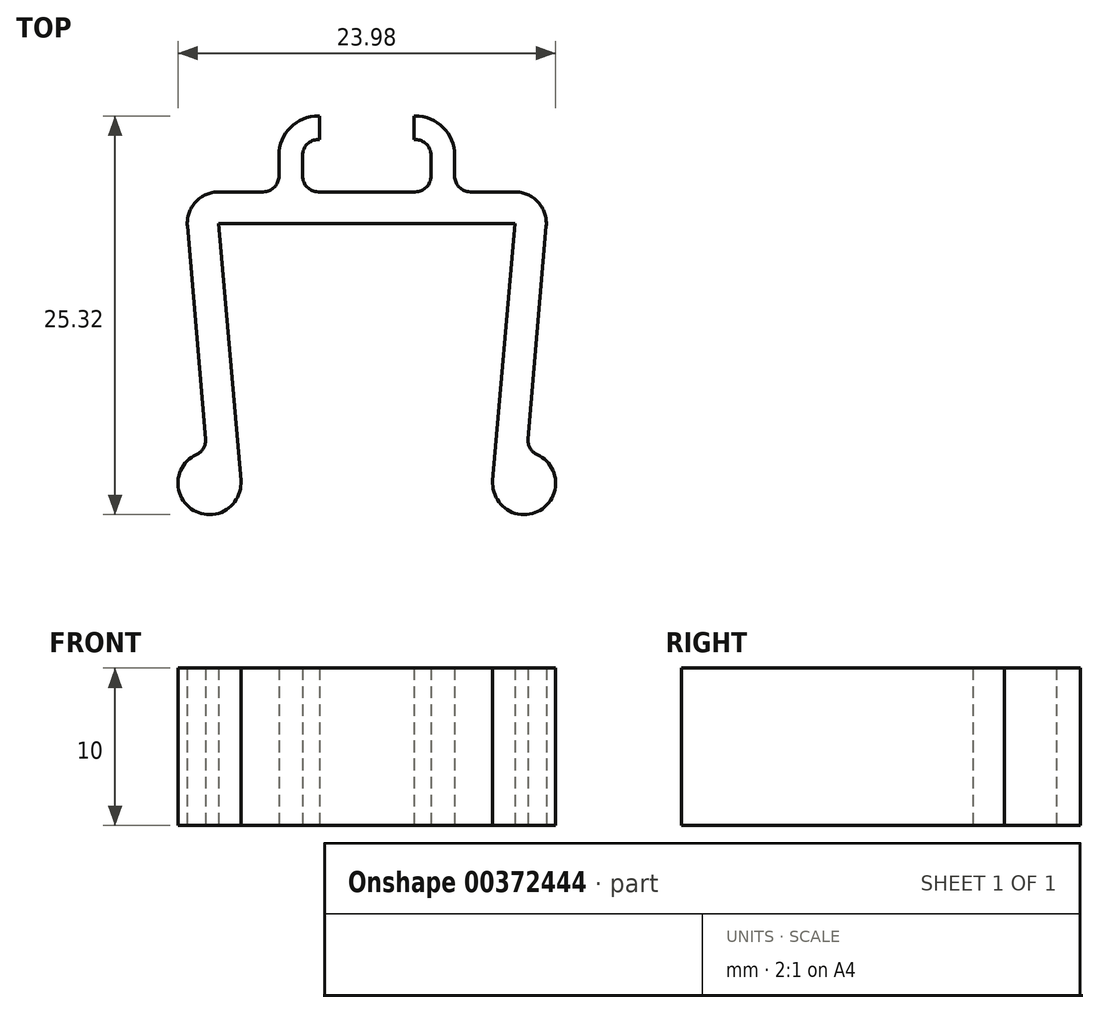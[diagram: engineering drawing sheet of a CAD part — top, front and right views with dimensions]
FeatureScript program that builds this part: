
annotation { "Feature Type Name" : "Feature", "Feature Type Description" : "" }
export const myFeature = defineFeature(function(context is Context, id is Id, definition is map)
    precondition{}
    {
        {
            var Q0;
            Q0=qCreatedBy(makeId("Top.planeOp"),FACE);
            var sketch = newSketch(context, id + "F0", { "sketchPlane" : qUnion([Q0])});
            skLineSegment(sketch, "E0.top", {"start": v(9.4, 7.19) * mm, "end": v(0, 7.19) * mm});
            skPoint(sketch, "E0.middle", {"position": v(0, 0) * mm});
            skLineSegment(sketch, "E1", {"start": v(0, 8.45) * mm, "end": v(0, -6.18) * mm, "construction": true});
            skLineSegment(sketch, "E2.MirrorCS", {"start": v(-9.4, 7.19) * mm, "end": v(0, 7.19) * mm});
            skLineSegment(sketch, "E3", {"start": v(9.4, 7.19) * mm, "end": v(8, -9.14) * mm});
            skLineSegment(sketch, "E4", {"start": v(0, 9.19) * mm, "end": v(3.08, 9.19) * mm});
            skLineSegment(sketch, "E5", {"start": v(11.4, 7.02) * mm, "end": v(10.23, -6.5) * mm});
            skArc(sketch, "E6", {"start": v(8, -9.14) * mm, "mid": v(11, -11.04) * mm, "end": v(10.82, -7.49) * mm});
            skPoint(sketch, "E7.visualSharp", {"position": v(11.58, 9.19) * mm});
            skArc(sketch, "E7.filletArc", {"start": v(11.4, 7.02) * mm, "mid": v(10.87, 8.54) * mm, "end": v(9.4, 9.19) * mm});
            skArc(sketch, "E8.MirrorCS", {"start": v(-8, -9.14) * mm, "mid": v(-11, -11.04) * mm, "end": v(-10.82, -7.49) * mm});
            skLineSegment(sketch, "E9.MirrorCS", {"start": v(-9.4, 7.19) * mm, "end": v(-8, -9.14) * mm});
            skLineSegment(sketch, "E10.MirrorCS", {"start": v(0, 9.19) * mm, "end": v(-3.08, 9.19) * mm});
            skLineSegment(sketch, "E11.MirrorCS", {"start": v(-11.4, 7.02) * mm, "end": v(-10.23, -6.5) * mm});
            skArc(sketch, "E12.MirrorCS", {"start": v(-11.4, 7.02) * mm, "mid": v(-10.87, 8.54) * mm, "end": v(-9.4, 9.19) * mm});
            skLineSegment(sketch, "E13", {"start": v(4.08, 10.19) * mm, "end": v(4.08, 11.51) * mm});
            skLineSegment(sketch, "E14", {"start": v(3.08, 12.51) * mm, "end": v(3, 12.51) * mm});
            skLineSegment(sketch, "E15", {"start": v(3, 12.51) * mm, "end": v(3, 14.01) * mm});
            skLineSegment(sketch, "E16", {"start": v(3, 14.01) * mm, "end": v(3.08, 14.01) * mm});
            skLineSegment(sketch, "E17", {"start": v(5.58, 11.51) * mm, "end": v(5.58, 10.19) * mm});
            skLineSegment(sketch, "E18.trimOffspring", {"start": v(6.58, 9.19) * mm, "end": v(9.4, 9.19) * mm});
            skPoint(sketch, "E19.visualSharp", {"position": v(5.58, 14.01) * mm});
            skArc(sketch, "E19.filletArc", {"start": v(5.58, 11.51) * mm, "mid": v(4.85, 13.28) * mm, "end": v(3.08, 14.01) * mm});
            skArc(sketch, "E20.filletArc", {"start": v(4.08, 11.51) * mm, "mid": v(3.78, 12.22) * mm, "end": v(3.08, 12.51) * mm});
            skLineSegment(sketch, "E21.MirrorCS", {"start": v(-3, 12.51) * mm, "end": v(-3, 14.01) * mm});
            skLineSegment(sketch, "E22.MirrorCS", {"start": v(-3, 14.01) * mm, "end": v(-3.08, 14.01) * mm});
            skLineSegment(sketch, "E23.MirrorCS", {"start": v(-3.08, 12.51) * mm, "end": v(-3, 12.51) * mm});
            skArc(sketch, "E24.MirrorCS", {"start": v(-4.08, 11.51) * mm, "mid": v(-3.78, 12.22) * mm, "end": v(-3.08, 12.51) * mm});
            skArc(sketch, "E25.MirrorCS", {"start": v(-5.58, 11.51) * mm, "mid": v(-4.85, 13.28) * mm, "end": v(-3.08, 14.01) * mm});
            skLineSegment(sketch, "E26.MirrorCS", {"start": v(-4.08, 10.19) * mm, "end": v(-4.08, 11.51) * mm});
            skLineSegment(sketch, "E27.MirrorCS", {"start": v(-5.58, 11.51) * mm, "end": v(-5.58, 10.19) * mm});
            skLineSegment(sketch, "E28.trimOffspring", {"start": v(-6.58, 9.19) * mm, "end": v(-9.4, 9.19) * mm});
            skPoint(sketch, "E29.visualSharp", {"position": v(-4.08, 9.19) * mm});
            skArc(sketch, "E29.filletArc", {"start": v(-4.08, 10.19) * mm, "mid": v(-3.78, 9.48) * mm, "end": v(-3.08, 9.19) * mm});
            skPoint(sketch, "E30.visualSharp", {"position": v(4.08, 9.19) * mm});
            skArc(sketch, "E30.filletArc", {"start": v(3.08, 9.19) * mm, "mid": v(3.78, 9.48) * mm, "end": v(4.08, 10.19) * mm});
            skPoint(sketch, "E31.visualSharp", {"position": v(5.58, 9.19) * mm});
            skArc(sketch, "E31.filletArc", {"start": v(5.58, 10.19) * mm, "mid": v(5.87, 9.48) * mm, "end": v(6.58, 9.19) * mm});
            skPoint(sketch, "E32.visualSharp", {"position": v(-5.58, 9.19) * mm});
            skArc(sketch, "E32.filletArc", {"start": v(-6.58, 9.19) * mm, "mid": v(-5.87, 9.48) * mm, "end": v(-5.58, 10.19) * mm});
            skPoint(sketch, "E33.visualSharp", {"position": v(-10.16, -7.32) * mm});
            skArc(sketch, "E33.filletArc", {"start": v(-10.82, -7.49) * mm, "mid": v(-10.37, -7.08) * mm, "end": v(-10.23, -6.5) * mm});
            skPoint(sketch, "E34.visualSharp", {"position": v(10.16, -7.32) * mm});
            skArc(sketch, "E34.filletArc", {"start": v(10.23, -6.5) * mm, "mid": v(10.37, -7.08) * mm, "end": v(10.82, -7.49) * mm});
            skSolve(sketch);
        }
        {
            var Q0;
            Q0=makeQuery(id+"F0.imprint","IMPRINT",FACE,{"disambiguationData":[TD([[makeQuery(id+"F0.imprint","IMPRINT",EDGE,{"derivedFrom":sQuery(id+"F0.wireOp",EDGE,"E0.top")}),-1.0]])]});
            extrude(context, id + "F1", {"entities" : qUnion([Q0]), "depth" : 10 * mm});
        }
    });
